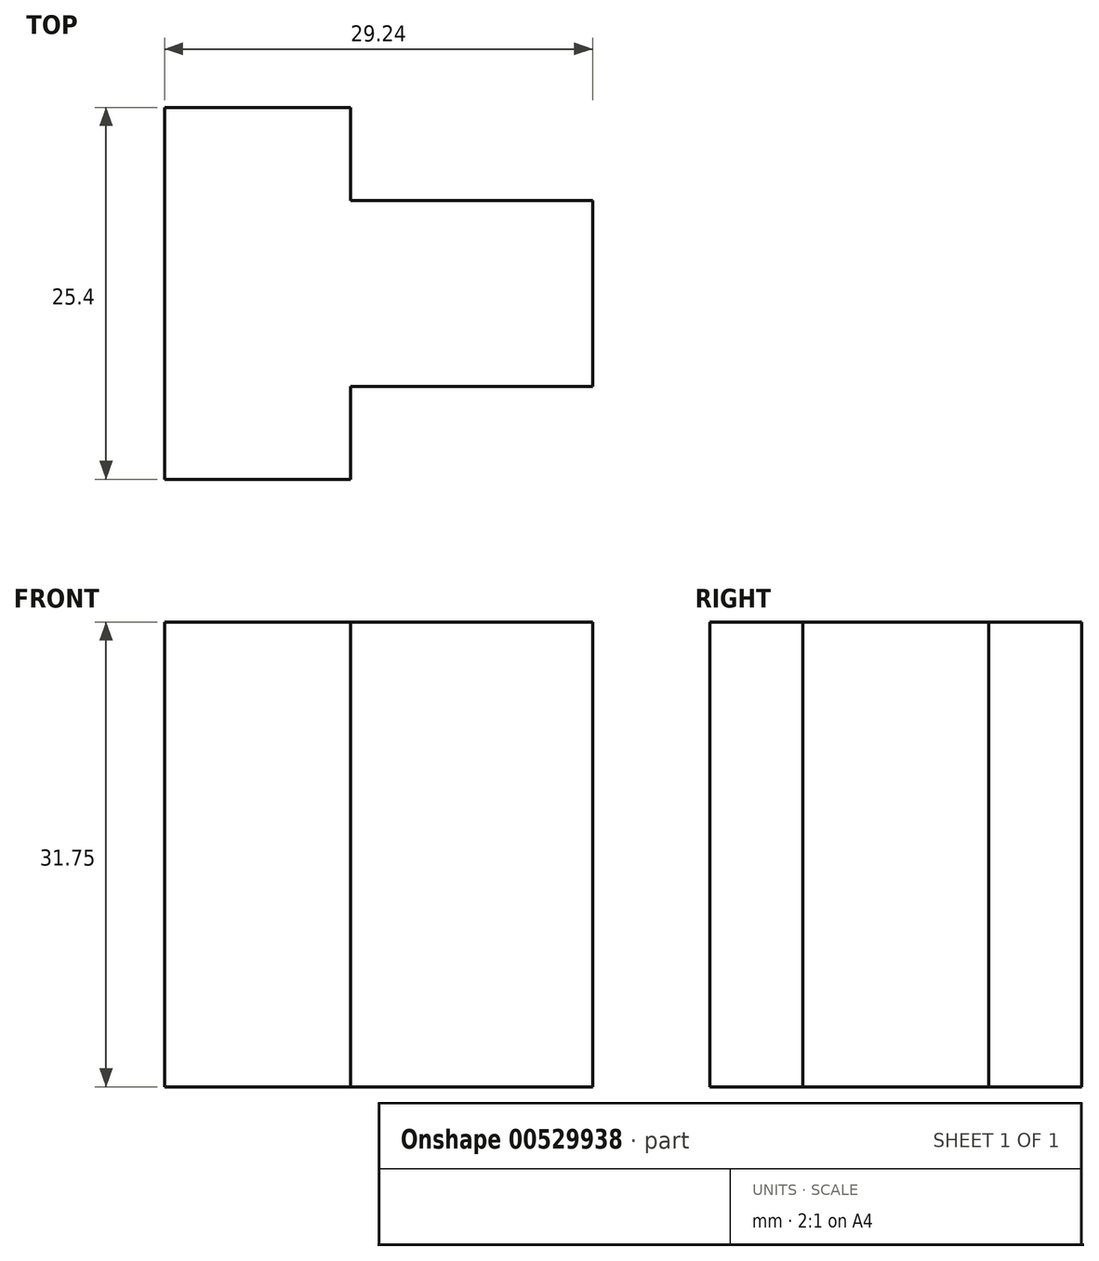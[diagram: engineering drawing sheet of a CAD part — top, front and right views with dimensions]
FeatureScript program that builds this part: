
annotation { "Feature Type Name" : "Feature", "Feature Type Description" : "" }
export const myFeature = defineFeature(function(context is Context, id is Id, definition is map)
    precondition{}
    {
        {
            var Q0;
            Q0=qCreatedBy(makeId("Top.planeOp"),FACE);
            var sketch = newSketch(context, id + "F0", { "sketchPlane" : qUnion([Q0])});
            skLineSegment(sketch, "E0", {"start": v(-19.82, 14.37) * mm, "end": v(-19.82, -11.03) * mm});
            skLineSegment(sketch, "E1", {"start": v(-19.82, -11.03) * mm, "end": v(-7.12, -11.03) * mm});
            skLineSegment(sketch, "E2", {"start": v(-19.82, 14.37) * mm, "end": v(-7.12, 14.37) * mm});
            skLineSegment(sketch, "E3", {"start": v(-7.12, 14.37) * mm, "end": v(-7.12, 8.02) * mm});
            skLineSegment(sketch, "E4", {"start": v(-7.12, 8.02) * mm, "end": v(9.42, 8.02) * mm});
            skLineSegment(sketch, "E5", {"start": v(9.42, 8.02) * mm, "end": v(9.42, -4.68) * mm});
            skLineSegment(sketch, "E6", {"start": v(9.42, -4.68) * mm, "end": v(-7.12, -4.68) * mm});
            skLineSegment(sketch, "E7", {"start": v(-7.12, -4.68) * mm, "end": v(-7.12, -11.03) * mm});
            skSolve(sketch);
        }
        {
            var Q0;
            Q0=makeQuery(id+"F0.imprint","IMPRINT",FACE,{"disambiguationData":[TD([[makeQuery(id+"F0.imprint","IMPRINT",EDGE,{"derivedFrom":sQuery(id+"F0.wireOp",EDGE,"E0")}),1.0]])]});
            extrude(context, id + "F1", {"entities" : qUnion([Q0]), "depth" : 31.75 * mm, "offsetDistance" : 25.4 * mm});
        }
    });
